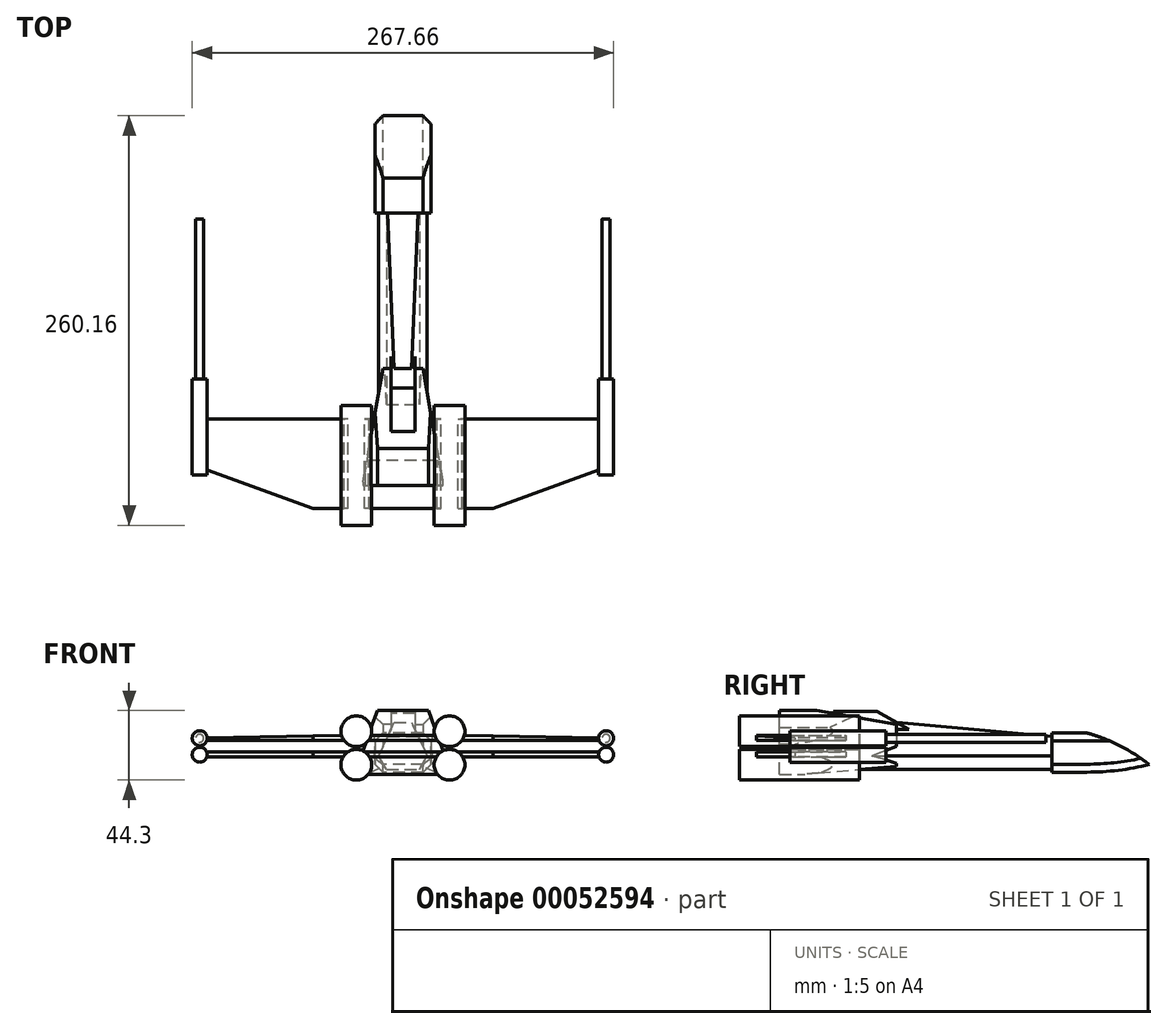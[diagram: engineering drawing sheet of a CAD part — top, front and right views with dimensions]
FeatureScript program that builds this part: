
annotation { "Feature Type Name" : "Feature", "Feature Type Description" : "" }
export const myFeature = defineFeature(function(context is Context, id is Id, definition is map)
    precondition{}
    {
        {
            var Q0;
            Q0=qCreatedBy(makeId("Right.planeOp"),FACE);
            var sketch = newSketch(context, id + "F0", { "sketchPlane" : qUnion([Q0])});
            skLineSegment(sketch, "E0.bottom", {"start": v(-69.86, 19.65) * mm, "end": v(57.8, 19.65) * mm});
            skLineSegment(sketch, "E0.top", {"start": v(-69.86, -11.17) * mm, "end": v(57.8, -11.17) * mm});
            skLineSegment(sketch, "E0.left", {"start": v(-69.86, 19.65) * mm, "end": v(-69.86, -11.17) * mm});
            skLineSegment(sketch, "E0.right", {"start": v(57.8, 19.65) * mm, "end": v(57.8, -11.17) * mm});
            skSolve(sketch);
        }
        {
            var Q0;
            Q0 = qSketchRegion(id + "F0", true);
            var Q1;
            Q1 = qSketchRegion(id + "F5", true);
            var Q2;
            Q2 = qSketchRegion(id + "F9", true);
            var Q3;
            Q3 = qSketchRegion(id + "F16", true);
            var Q4;
            Q4 = qSketchRegion(id + "F18", true);
            var Q5;
            Q5 = qSketchRegion(id + "F23", true);
            var Q6;
            Q6 = qSketchRegion(id + "F25", true);
            var Q7;
            Q7 = qSketchRegion(id + "F26", true);
            extrude(context, id + "F1", {"entities" : qUnion([Q0, Q1, Q2, Q3, Q4, Q5, Q6, Q7]), "depth" : 17.78 * mm});
        }
        {
            var Q0;
            Q0=makeQuery(id+"F1.opExtrude","CAP_EDGE",EDGE,{"disambiguationData":[OSD([sQuery(id+"F0.wireOp",EDGE,"E0.top")])],"isStart":false});
            chamfer(context, id + "F2", {"entities" : qUnion([Q0]), "chamferType" : ChamferType.OFFSET_ANGLE, "width" : 12.7 * mm, "oppositeDirection" : false, "angle" : 30 * degree, "tangentPropagation" : true});
        }
        {
            var Q0;
            Q0=makeQuery(id+"F1.opExtrude","CAP_EDGE",EDGE,{"disambiguationData":[OSD([sQuery(id+"F0.wireOp",EDGE,"E0.bottom")])],"isStart":false});
            chamfer(context, id + "F3", {"entities" : qUnion([Q0]), "chamferType" : ChamferType.OFFSET_ANGLE, "width" : 12.7 * mm, "oppositeDirection" : false, "angle" : 65 * degree, "tangentPropagation" : true});
        }
        {
            var Q0;
            Q0=makeQuery(id+"F1.opExtrude","SWEPT_EDGE",EDGE,{"disambiguationData":[OSD([sQuery(id+"F0.wireOp",EDGE,"E0.bottom"),sQuery(id+"F0.wireOp",EDGE,"E0.right")])]});
            chamfer(context, id + "F4", {"entities" : qUnion([Q0]), "chamferType" : ChamferType.OFFSET_ANGLE, "width" : 127 * mm, "oppositeDirection" : false, "angle" : 5 * degree, "tangentPropagation" : true});
        }
        {
            var Q0;
            Q0=qCreatedBy(makeId("Right.planeOp"),FACE);
            var sketch = newSketch(context, id + "F5", { "sketchPlane" : qUnion([Q0])});
            skLineSegment(sketch, "E1.bottom", {"start": v(42.17, 11.96) * mm, "end": v(64.54, 11.96) * mm});
            skLineSegment(sketch, "E1.top", {"start": v(42.17, -12.94) * mm, "end": v(64.54, -12.94) * mm});
            skLineSegment(sketch, "E1.left", {"start": v(42.17, 11.96) * mm, "end": v(42.17, -12.94) * mm});
            skArc(sketch, "E2", {"start": v(104.1, -8.1) * mm, "mid": v(85.34, 3.94) * mm, "end": v(64.54, 11.96) * mm});
            skArc(sketch, "E3", {"start": v(64.54, -12.94) * mm, "mid": v(84.47, -11.72) * mm, "end": v(104.1, -8.1) * mm});
            skSolve(sketch);
        }
        {
            var Q0;
            Q0 = qSketchRegion(id + "F5", true);
            extrude(context, id + "F6", {"entities" : qUnion([Q0]), "operationType" : NewBodyOperationType.ADD, "depth" : 17.78 * mm});
        }
        {
            var Q0;
            Q0=makeQuery(id+"F6.opExtrude","CAP_EDGE",EDGE,{"disambiguationData":[OSD([sQuery(id+"F5.wireOp",EDGE,"E1.bottom")])],"isStart":false});
            chamfer(context, id + "F7", {"entities" : qUnion([Q0]), "width" : 5.08 * mm, "tangentPropagation" : true});
        }
        {
            var Q0;
            Q0=makeQuery(id+"F6.opExtrude","CAP_EDGE",EDGE,{"disambiguationData":[OSD([sQuery(id+"F5.wireOp",EDGE,"E1.top")])],"isStart":false});
            chamfer(context, id + "F8", {"entities" : qUnion([Q0]), "width" : 5.08 * mm, "tangentPropagation" : true});
        }
        {
            var Q0;
            Q0=qCreatedBy(makeId("Right.planeOp"),FACE);
            var sketch = newSketch(context, id + "F9", { "sketchPlane" : qUnion([Q0])});
            skLineSegment(sketch, "E4.bottom", {"start": v(-56.43, 26.33) * mm, "end": v(-130.66, 26.33) * mm});
            skLineSegment(sketch, "E4.top", {"start": v(-56.43, -14.26) * mm, "end": v(-130.66, -14.26) * mm});
            skLineSegment(sketch, "E4.left", {"start": v(-56.43, 26.33) * mm, "end": v(-56.43, -14.26) * mm});
            skLineSegment(sketch, "E4.right", {"start": v(-130.66, 26.33) * mm, "end": v(-130.66, -14.26) * mm});
            skSolve(sketch);
        }
        {
            var Q0;
            Q0=makeQuery(id+"F9.imprint","IMPRINT",FACE,{"disambiguationData":[TD([[makeQuery(id+"F9.imprint","IMPRINT",EDGE,{"derivedFrom":sQuery(id+"F9.wireOp",EDGE,"E4.bottom")}),1.0]])]});
            extrude(context, id + "F10", {"entities" : qUnion([Q0]), "operationType" : NewBodyOperationType.ADD, "depth" : 25.4 * mm});
        }
        {
            var Q0;
            Q0=makeQuery(id+"F10.opExtrude","SWEPT_EDGE",EDGE,{"disambiguationData":[OSD([sQuery(id+"F9.wireOp",EDGE,"E4.bottom"),sQuery(id+"F9.wireOp",EDGE,"E4.left")])]});
            chamfer(context, id + "F11", {"entities" : qUnion([Q0]), "chamferType" : ChamferType.OFFSET_ANGLE, "width" : 50.8 * mm, "oppositeDirection" : false, "angle" : 10 * degree, "tangentPropagation" : true});
        }
        {
            var Q0;
            Q0=makeQuery(id+"F10.opExtrude","CAP_EDGE",EDGE,{"disambiguationData":[OSD([sQuery(id+"F9.wireOp",EDGE,"E4.bottom")])],"isStart":false});
            chamfer(context, id + "F12", {"entities" : qUnion([Q0]), "chamferType" : ChamferType.OFFSET_ANGLE, "width" : 25.4 * mm, "oppositeDirection" : false, "angle" : 20 * degree, "tangentPropagation" : true});
        }
        {
            var Q0;
            Q0=makeQuery(id+"F10.opExtrude","CAP_EDGE",EDGE,{"disambiguationData":[OSD([sQuery(id+"F9.wireOp",EDGE,"E4.left")])],"isStart":false});
            chamfer(context, id + "F13", {"entities" : qUnion([Q0]), "chamferType" : ChamferType.OFFSET_ANGLE, "width" : 12.7 * mm, "oppositeDirection" : false, "angle" : 80 * degree, "tangentPropagation" : true});
        }
        {
            var Q0;
            Q0=makeQuery(id+"F10.opExtrude","SWEPT_EDGE",EDGE,{"disambiguationData":[OSD([sQuery(id+"F9.wireOp",EDGE,"E4.top"),sQuery(id+"F9.wireOp",EDGE,"E4.left")])]});
            chamfer(context, id + "F14", {"entities" : qUnion([Q0]), "chamferType" : ChamferType.OFFSET_ANGLE, "width" : 5.08 * mm, "oppositeDirection" : false, "angle" : 85 * degree, "tangentPropagation" : true});
        }
        {
            var Q0;
            Q0=makeQuery(id+"F10.opExtrude","SWEPT_FACE",FACE,{"disambiguationData":[OSD([sQuery(id+"F9.wireOp",EDGE,"E4.right")])]});
            cPlane(context, id + "F15", {"entities" : qUnion([Q0]), "cplaneType" : CPlaneType.OFFSET, "offset" : 0 * mm, "width" : 152.4 * mm, "height" : 152.4 * mm});
        }
        {
            var Q0;
            Q0=qCreatedBy(id+"F15.planeOp",FACE);
            var sketch = newSketch(context, id + "F16", { "sketchPlane" : qUnion([Q0])});
            skCircle(sketch, "E5", {"center": v(29.6, 13.03) * mm, "radius": 9.75 * mm});
            skCircle(sketch, "E6", {"center": v(29.6, -8.22) * mm, "radius": 9.75 * mm});
            skSolve(sketch);
        }
        {
            var Q0;
            Q0 = qSketchRegion(id + "F16", true);
            extrude(context, id + "F17", {"entities" : qUnion([Q0]), "operationType" : NewBodyOperationType.ADD, "depth" : 25.4 * mm, "hasSecondDirection" : true, "secondDirectionOppositeDirection" : true, "secondDirectionDepth" : 50.8 * mm});
        }
        {
            var Q0;
            Q0=qCreatedBy(makeId("Right.planeOp"),FACE);
            var sketch = newSketch(context, id + "F18", { "sketchPlane" : qUnion([Q0])});
            skLineSegment(sketch, "E7.bottom", {"start": v(-145.4, 10.5) * mm, "end": v(-88.38, 10.5) * mm});
            skLineSegment(sketch, "E7.top", {"start": v(-145.4, 7.37) * mm, "end": v(-88.38, 7.37) * mm});
            skLineSegment(sketch, "E7.left", {"start": v(-145.4, 10.5) * mm, "end": v(-145.4, 7.37) * mm});
            skLineSegment(sketch, "E7.right", {"start": v(-88.38, 10.5) * mm, "end": v(-88.38, 7.37) * mm});
            skLineSegment(sketch, "E8.bottom", {"start": v(-145.4, 0) * mm, "end": v(-88.38, 0) * mm});
            skLineSegment(sketch, "E8.top", {"start": v(-145.4, -3.14) * mm, "end": v(-88.38, -3.14) * mm});
            skLineSegment(sketch, "E8.left", {"start": v(-145.4, 0) * mm, "end": v(-145.4, -3.14) * mm});
            skLineSegment(sketch, "E8.right", {"start": v(-88.38, 0) * mm, "end": v(-88.38, -3.14) * mm});
            skSolve(sketch);
        }
        {
            var Q0;
            Q0 = qSketchRegion(id + "F18", true);
            extrude(context, id + "F19", {"entities" : qUnion([Q0]), "operationType" : NewBodyOperationType.ADD, "depth" : 127 * mm});
        }
        {
            var Q0;
            Q0=makeQuery(id+"F19.opExtrude","CAP_EDGE",EDGE,{"disambiguationData":[OSD([sQuery(id+"F18.wireOp",EDGE,"E7.bottom")])],"isStart":false});
            chamfer(context, id + "F20", {"entities" : qUnion([Q0]), "chamferType" : ChamferType.OFFSET_ANGLE, "width" : 101.6 * mm, "oppositeDirection" : false, "angle" : 1 * degree, "tangentPropagation" : true});
        }
        {
            var Q0;
            Q0=makeQuery(id+"F19.opExtrude","CAP_EDGE",EDGE,{"disambiguationData":[OSD([sQuery(id+"F18.wireOp",EDGE,"E7.left")])],"isStart":false});
            var Q1;
            Q1=makeQuery(id+"F19.opExtrude","CAP_EDGE",EDGE,{"disambiguationData":[OSD([sQuery(id+"F18.wireOp",EDGE,"E8.left")])],"isStart":false});
            chamfer(context, id + "F21", {"entities" : qUnion([Q0, Q1]), "chamferType" : ChamferType.OFFSET_ANGLE, "width" : 25.4 * mm, "oppositeDirection" : false, "angle" : 70 * degree, "tangentPropagation" : true});
        }
        {
            var Q0;
            {var subQ0=sQuery(id+"F18.wireOp",EDGE,"E8.bottom");var subQ1=sQuery(id+"F18.wireOp",EDGE,"E8.right");var subQ2=sQuery(id+"F18.wireOp",EDGE,"E8.top");Q0=makeQuery(id+"F19.boolean.opBoolean","SPLIT",FACE,{"disambiguationData":[TD([makeQuery(id+"F19.opExtrude","CAP_FACE",FACE,{"disambiguationData":[OSD([subQ0,subQ2,sQuery(id+"F18.wireOp",EDGE,"E8.left"),subQ1])],"isStart":false})])],"derivedFrom":makeQuery(id+"F19.opExtrude","SWEPT_FACE",FACE,{"disambiguationData":[OSD([subQ1])]})});}
            cPlane(context, id + "F22", {"entities" : qUnion([Q0]), "cplaneType" : CPlaneType.OFFSET, "offset" : 0 * mm, "width" : 152.4 * mm, "height" : 152.4 * mm});
        }
        {
            var Q0;
            Q0=qCreatedBy(id+"F22.planeOp",FACE);
            var sketch = newSketch(context, id + "F23", { "sketchPlane" : qUnion([Q0])});
            skCircle(sketch, "E9", {"center": v(-129.07, 8.63) * mm, "radius": 4.77 * mm});
            skCircle(sketch, "E10", {"center": v(-129.07, -1.82) * mm, "radius": 4.77 * mm});
            skSolve(sketch);
        }
        {
            var Q0;
            Q0 = qSketchRegion(id + "F23", true);
            extrude(context, id + "F24", {"entities" : qUnion([Q0]), "operationType" : NewBodyOperationType.ADD, "depth" : 25.4 * mm, "hasSecondDirection" : true, "secondDirectionOppositeDirection" : true, "secondDirectionDepth" : 35.56 * mm});
        }
        {
            var Q0;
            Q0=makeQuery(id+"F24.opExtrude","CAP_FACE",FACE,{"disambiguationData":[OSD([sQuery(id+"F23.wireOp",EDGE,"E9")])],"isStart":false});
            var sketch = newSketch(context, id + "F25", { "sketchPlane" : qUnion([Q0])});
            skCircle(sketch, "E11", {"center": v(-129.07, 8.63) * mm, "radius": 2.54 * mm});
            skSolve(sketch);
        }
        {
            var Q0;
            Q0=makeQuery(id+"F24.opExtrude","CAP_FACE",FACE,{"disambiguationData":[OSD([sQuery(id+"F23.wireOp",EDGE,"E10")])],"isStart":false});
            var sketch = newSketch(context, id + "F26", { "sketchPlane" : qUnion([Q0])});
            skCircle(sketch, "E12", {"center": v(-129.07, -1.82) * mm, "radius": 2.54 * mm});
            skSolve(sketch);
        }
        {
            var Q0;
            Q0=makeQuery(id+"F25.imprint","IMPRINT",FACE,{"disambiguationData":[TD([[makeQuery(id+"F25.imprint","IMPRINT",EDGE,{"derivedFrom":sQuery(id+"F25.wireOp",EDGE,"E11")}),1.0]])]});
            var Q1;
            Q1=sQuery(id+"F25.wireOp",EDGE,"E11");
            extrude(context, id + "F27", {"entities" : qUnion([Q0]), "surfaceEntities" : qUnion([Q1]), "depth" : 101.6 * mm});
        }
        {
            var Q0;
            Q0=sQuery(id+"F26.wireOp",EDGE,"E12");
            extrude(context, id + "F28", {"bodyType" : ToolBodyType.SURFACE, "surfaceEntities" : qUnion([Q0]), "depth" : 101.6 * mm});
        }
        {
            var Q0;
            Q0=makeQuery(id+"F1.opExtrude","SWEPT_BODY",BODY,{"disambiguationData":[OSD([sQuery(id+"F0.wireOp",EDGE,"E0.bottom"),sQuery(id+"F0.wireOp",EDGE,"E0.top"),sQuery(id+"F0.wireOp",EDGE,"E0.left"),sQuery(id+"F0.wireOp",EDGE,"E0.right")])]});
            var Q1;
            Q1=makeQuery(id+"F27.opExtrude","SWEPT_BODY",BODY,{"disambiguationData":[OSD([sQuery(id+"F25.wireOp",EDGE,"E11")])]});
            var Q2;
            Q2=qCreatedBy(makeId("Right.planeOp"),FACE);
            mirror(context, id + "F29", {"operationType" : NewBodyOperationType.ADD, "entities" : qUnion([Q0, Q1]), "mirrorPlane" : qUnion([Q2])});
        }
        {
            var Q0;
            Q0=makeQuery(id+"F28.opExtrude","SWEPT_BODY",BODY,{"disambiguationData":[OSD([sQuery(id+"F26.wireOp",EDGE,"E12")])]});
            var Q1;
            Q1=qCreatedBy(makeId("Right.planeOp"),FACE);
            mirror(context, id + "F30", {"entities" : qUnion([Q0]), "mirrorPlane" : qUnion([Q1])});
        }
        {
            var Q0;
            Q0=qCreatedBy(makeId("Right.planeOp"),FACE);
            var sketch = newSketch(context, id + "F31", { "sketchPlane" : qUnion([Q0])});
            skLineSegment(sketch, "E13.bottom", {"start": v(-96.39, 25.56) * mm, "end": v(-68.71, 25.56) * mm});
            skLineSegment(sketch, "E13.top", {"start": v(-96.39, 4.9) * mm, "end": v(-68.71, 4.9) * mm});
            skLineSegment(sketch, "E13.left", {"start": v(-96.39, 25.56) * mm, "end": v(-96.39, 4.9) * mm});
            skLineSegment(sketch, "E14", {"start": v(-68.71, 25.56) * mm, "end": v(-34.2, 6) * mm});
            skLineSegment(sketch, "E15", {"start": v(-34.2, 6) * mm, "end": v(-68.71, 4.9) * mm});
            skSolve(sketch);
        }
        {
            var Q0;
            Q0 = qSketchRegion(id + "F31", true);
            extrude(context, id + "F32", {"entities" : qUnion([Q0]), "operationType" : NewBodyOperationType.ADD, "depth" : 7.62 * mm, "hasSecondDirection" : true, "secondDirectionOppositeDirection" : true, "secondDirectionDepth" : 7.62 * mm});
        }
    });
